# Revit family: KFL1
name_source: partatom
category: Lighting Fixtures
revit_build: Autodesk Revit 2014 (Build: 20130308_1515(x64)
units: mm (PartAtom-declared; Revit-internal decimal feet)

## types (1)
- KFL1-6L
    Apparent Load = 8 VA
    Assembly Code = D5020200
    Certifications = UL 1598 , IP66 certified, UL 8750
    Color Filter = 16777215
    Connector Description = Lighting Connector
    Default Elevation = 48 "
    Description = The Kim Archictural Flood is a striking timeless form seamlessly blends high performance optics, controls, scalability and architectural mounting options that cover a wide variety of applications and enhance their environment.
    Dimming Lamp Color Temperature Shift = <None>
    Features = Second generation LED 2.0
7 beam patterns, Narrow Spot, Spot, Narrow, Medium, Medium Flood, Horizontal and Vertical distributions generate high efficiencies and outstanding uniformity of illumination.
Die-cast housing with integral cooling ribs promote efficient transfer of heat.
Thoughtfully designed mounting accessories thatintegrate into the fixture design.
IP66 sealed optical chamber.
Standard 20kV surge suppression
Broad offering of wireless control options available forperfectly tailored lighting and ability to meet stringentcode requirements.
    Housing Material = Paint - Hubbell - Carbon Black
    LED = KF : KL-8LED
    Lamp = LED
    Length = 26.38 "
    Light DIstributin = Narrow Spot,Spot,Narrow,Medium,Medium Flood,Wide Flood,Horizonal Flood,Vertical Flood
    Load Classification = Lighting
    Manufacturer = Kim Lighting
    Model = KFL1RGBW
    Photometric Note = For more ies file please find the above Photometric Web Link
    Photometric Web File = KFL1-6L-8-RGBW-HF.ies
    Photometric Web Link = https://www.hubbell.com
    Power Factor = 1
    Product Doucmentation Link = https://hubbellcdn.com
    Product Page URL = https://www.hubbell.com
    Reflector Finish = Hubbell - White Glass
    Tilt Angle = 0.00°
    URL = https://www.hubbell.com
    Voltage = 120 V
    Warranty = 5 years Warranty
    Wattage Comments = 8W
    Watts = 8 W
    Width = 11.63 "
    Width 1 = 5 "

## geometry (parser evidence)
native form markers: Sweep x5
no freeform markers — native parametric forms only
